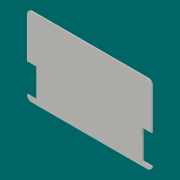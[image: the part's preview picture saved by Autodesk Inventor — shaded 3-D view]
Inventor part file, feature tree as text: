
AUTODESK INVENTOR PART (.ipt)
format: ipt  version: 2016 (Build 200138000, 138)  size: 149,504 bytes
history: native  units: mm
features: extrude x3, sketch x3, other x1, fillet x1, mirror x1, projected_geometry x1
ambient origin geometry x8: Origin, YZ Plane, XZ Plane, XY Plane, X Axis, Y Axis, Z Axis, Center Point
bodies: Solid1 (feature_tree)
feature tree (10):
  other  "<userpath>\OneDrive\projects\splitFlapDisplay\parameters.xlsx"
  extrude  "Extrusion1"  Depth=53.98mm
  fillet  "Fillet1"  Radius=0.76mm
  extrude  "Extrusion2"  Depth=2.88mm
  extrude  "Extrusion3"  Depth=6.35mm
  mirror  "Mirror1"
  sketch  "Sketch1"  dims[d0=85.6mm d1=53.98mm d2=0.76mm]
  sketch  "Sketch2"  dims[d3=0.0mm d4=2.88mm]
  projected_geometry  "Projected Loop1"
  sketch  "Sketch3"  dims[d5=6.35mm d6=6.35mm d7=3.0mm d8=3.0mm d9=20.0mm d10=20.0mm d11=0.76mm d12=0.0mm d13=3.0mm d14=3.0mm d15=0.76mm d16=1.5mm d17=1.5mm d18=1.5mm d19=0.76mm d20=0.0mm]
